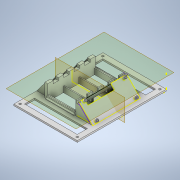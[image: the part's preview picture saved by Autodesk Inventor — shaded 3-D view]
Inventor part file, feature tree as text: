
AUTODESK INVENTOR PART (.ipt)
format: ipt  version: 2020.1 (Build 241239000, 239)  size: 666,624 bytes
history: native  units: mm
features: sketch x37, extrude x23, projected_geometry x16, chamfer x4, mirror x4, plane x3, hole x1, pattern_linear x1
ambient origin geometry x8: Origin, YZ Plane, XZ Plane, XY Plane, X Axis, Y Axis, Z Axis, Center Point
bodies: Solid1 (feature_tree)
feature tree (89):
  extrude  "Extrusion1"  Depth=168.0mm
  sketch  "Sketch2"  dims[d4=3.0mm d5=0.0mm d6=90.0mm]
  extrude  "Extrusion2"  Depth=90.0mm
  chamfer  "Chamfer1"  Distance=40.0mm
  sketch  "Sketch4"  dims[d8=20.0mm]
  extrude  "Extrusion3"  Depth=3.0mm
  sketch  "Sketch8"  dims[d10=39.0mm]
  extrude  "Extrusion5"  Depth=3.0mm
  sketch  "Sketch9"  dims[d11=39.0mm d12=40.0mm d13=0.0mm]
  sketch  "Sketch10"  dims[d14=40.0mm d15=2.0mm d16=45.0deg d17=3.0mm]
  sketch  "Sketch11"  dims[d18=3.0mm d19=3.0mm]
  extrude  "Extrusion6"  Depth=31.0mm
  extrude  "Extrusion7"  Depth=75.0mm
  extrude  "Extrusion8"  Depth=90.0mm
  sketch  "Sketch15"  dims[d26=7.5mm d27=0.0mm]
  sketch  "Sketch17"  dims[d28=3.0mm d29=0.0mm]
  sketch  "Sketch18"  dims[d30=34.0mm d31=3.0mm]
  sketch  "Sketch19"  dims[d32=300.0mm d33=0.0mm d37=5.0mm]
  extrude  "Extrusion10"  TaperAngle=0.0deg  [1 undecoded]
  extrude  "Extrusion11"  TaperAngle=0.0deg  [1 undecoded]
  extrude  "Extrusion12"  Depth=3.0mm
  extrude  "Extrusion13"  Depth=5.0mm
  extrude  "Extrusion14"  Depth=5.0mm
  hole  "Hole1"  [1 undecoded]
  extrude  "Extrusion16"  Depth=5.4185mm
  chamfer  "Chamfer2"  Distance=40.0mm
  extrude  "Extrusion17"  Depth=90.0mm
  extrude  "Extrusion18"  Depth=90.0mm
  plane  "Work Plane1"
  mirror  "Mirror1"
  extrude  "Extrusion19"  Depth=2.0mm
  sketch  "Sketch31"  dims[d78=10.0mm d79=0.0mm]
  extrude  "Extrusion20"  Depth=10.0mm TaperAngle=0.0deg
  pattern_linear  "Rectangular Pattern1"  Count1=5  [1 undecoded]
  plane  "Work Plane2"
  sketch  "Sketch36"  dims[d82=10.0mm d83=0.0mm d84=20.0mm d85=50.0mm d86=0.0mm d87=0.0mm d88=20.0mm d89=0.0mm]
  extrude  "Extrusion23"  Depth=20.0mm TaperAngle=0.0deg
  chamfer  "Chamfer4"  Distance=20.0mm
  mirror  "Mirror2"
  extrude  "Extrusion24"  Depth=6.0mm
  mirror  "Mirror3"
  extrude  "Extrusion26"  Depth=5.0mm
  extrude  "Extrusion27"  Depth=1.5mm
  extrude  "Extrusion28"  Depth=5.0mm TaperAngle=0.0deg
  sketch  "Sketch43"  dims[d114=20.0mm d115=26.613mm d116=45.0deg d117=5.0mm d118=0.0mm d119=3.0mm d120=0.0mm]
  sketch  "Sketch48"  dims[d121=5.0mm d122=0.0mm]
  plane  "Work Plane3"
  extrude  "Extrusion31"  Depth=5.0mm TaperAngle=0.0deg
  chamfer  "Chamfer6"  Distance=3.0mm
  mirror  "Mirror4"
  sketch  "Sketch1"  dims[d2=120.0mm d3=168.0mm]
  sketch  "Sketch3"  dims[d7=90.0mm]
  sketch  "Sketch5"  dims[d9=10.0mm]
  sketch  "Sketch12"  dims[d20=3.0mm d21=31.0mm]
  sketch  "Sketch13"  dims[d22=31.0mm d23=75.0mm]
  sketch  "Sketch14"  dims[d24=75.0mm d25=90.0mm]
  projected_geometry  "Projected Loop1"
  projected_geometry  "Projected Loop2"
  projected_geometry  "Projected Loop3"
  sketch  "Sketch20"  dims[d38=5.0mm d39=5.0mm]
  projected_geometry  "Projected Loop4"
  sketch  "Sketch21"  dims[d40=5.0mm d41=5.0mm d42=0.0mm]
  projected_geometry  "Projected Loop5"
  sketch  "Sketch22"  dims[d43=53.0mm d44=5.4185mm]
  sketch  "Sketch23"  dims[d45=5.418567mm]
  sketch  "Sketch24"  dims[d46=0.0mm]
  sketch  "Sketch26"  dims[d47=90.0mm d48=40.0mm d49=0.0mm]
  projected_geometry  "Projected Loop6"
  sketch  "Sketch27"  dims[d50=10.0mm d51=90.0mm]
  sketch  "Sketch28"  dims[d52=10.0mm d53=90.0mm d55=10.0mm d56=10.0mm d58=10.0mm]
  projected_geometry  "Projected Loop7"
  sketch  "Sketch29"  dims[d60=5.0mm d61=0.0mm d62=2.0mm]
  projected_geometry  "Projected Loop8"
  sketch  "Sketch30"  dims[d63=0.0mm d64=0.0mm d76=10.0mm d77=0.0mm]
  projected_geometry  "Projected Loop9"
  sketch  "Sketch32"  dims[d80=10.0mm d81=50.0mm]
  sketch  "Sketch37"  dims[d92=6.0mm]
  sketch  "Sketch38"  dims[d93=4.0mm d94=6.0mm d95=8.4mm d96=2.0mm d97=90.0deg d98=8.0mm d99=20.594885mm d100=6.0mm]
  projected_geometry  "Projected Loop14"
  sketch  "Sketch40"  dims[d101=180.0deg d102=5.0mm]
  projected_geometry  "Projected Loop16"
  sketch  "Sketch41"  dims[d103=5.0mm d104=1.5mm]
  projected_geometry  "Projected Loop17"
  sketch  "Sketch42"  dims[d105=50.0mm d107=20.0mm d108=10.0mm d110=10.0mm d112=5.0mm d113=0.0mm]
  projected_geometry  "Projected Loop18"
  projected_geometry  "Projected Loop19"
  projected_geometry  "Projected Loop20"
  sketch  "Sketch49"  dims[d123=2.0mm d124=10.543mm d125=5.0mm d126=0.0mm d127=40.0mm d129=29.333333mm d138=3.0mm d139=4.0mm d140=0.0mm d144=2.0mm d145=2.0mm d146=45.0deg d147=2.0mm d148=0.0mm d157=13.0mm d158=2.0mm d159=0.0mm d160=0.0mm d167=10.0mm d168=10.0mm d169=0.0mm d170=0.05mm d171=0.25mm d172=41.581mm d173=0.0mm d184=1.5mm d185=2.0mm d186=3.0mm d187=0.0mm d188=1.5mm d189=2.0mm d190=45.0deg d73=0.5mm d74=0.872665mm d75=0.5mm d106=0.872665mm d153=0.5mm d154=0.872665mm d155=0.5mm d156=0.872665mm d176=0.872665mm d177=0.872665mm]
  projected_geometry  "Projected Loop21"
note: 4 required parameter values undecoded (feature->parameter linkage not recoverable at this tier; creation-order binding heuristic only, values carry confidence <= 0.55)
